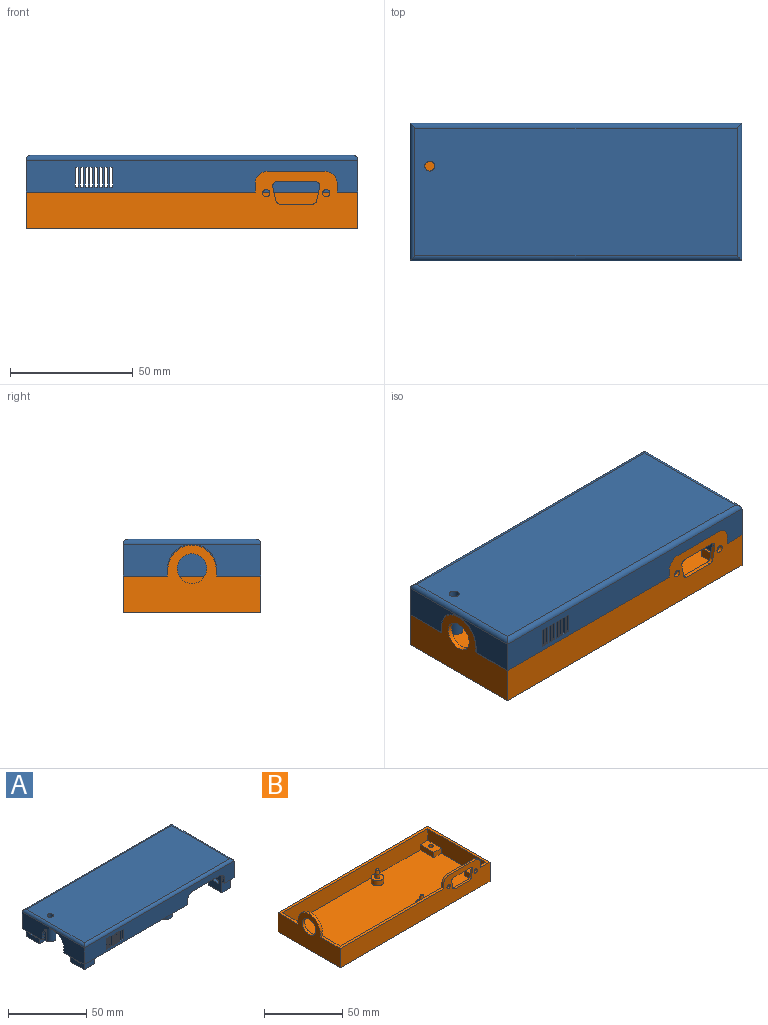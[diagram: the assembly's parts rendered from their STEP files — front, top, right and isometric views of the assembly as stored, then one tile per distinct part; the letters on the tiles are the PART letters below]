
ASSEMBLY  parts=2 mates=1
PART A: 184 faces, bbox 135x56x24 mm
  f0: plane 12x6mm, normal (-1,0,0), area 57.2mm2, adj f16,f36,f37,f132,f133,f134,f151
  f1: plane 12x6mm, normal (-1,0,0), area 57.2mm2, adj f8,f40,f41,f137,f138,f139,f156
  f2: cylinder r=1.55mm len=3.4mm, axis (0,0,-1), area 33.1mm2, adj f137,f155
  f3: cylinder r=1.55mm len=3.4mm, axis (0,0,-1), area 33.1mm2, adj f132,f150
  f4: plane 21x12mm, normal (-1,0,0), area 237.2mm2, adj f11,f19,f113,f114,f120,f121,f124,f125
  f5: plane 21x12.52mm, normal (-1,0,0), area 248mm2, adj f10,f19,f116,f118,f126,f127,f128,f129
  f6: cylinder r=1.6mm len=5.4mm, axis (0,0,1), area 54.3mm2, adj f128,f160
  f7: cylinder r=1.6mm len=5.4mm, axis (0,0,1), area 54.3mm2, adj f124,f165
  f8: plane 135x56mm, normal (0,0,-1), area 435.6mm2, adj f1,f9,f10,f12,f13,f14,f15,f17
  f9: plane 27.48x13mm, normal (-1,0,0), area 357.3mm2, adj f8,f19,f113,f118
  f10: plane 114.5x13mm, normal (0,-1,0), area 1411.7mm2, adj f5,f8,f19,f42,f80,f81,f82,f83
  f11: plane 114.5x13mm, normal (0,1,0), area 1144.9mm2, adj f4,f16,f19,f23,f25,f26,f27,f38
  f12: plane 135x13mm, normal (0,1,0), area 1678.2mm2, adj f8,f15,f17,f28,f80,f81,f82,f83
  f13: plane 135x13mm, normal (0,-1,0), area 1408.4mm2, adj f8,f15,f16,f17,f23,f24,f25,f26
  f14: plane 28x13mm, normal (1,0,0), area 158mm2, adj f8,f16,f19,f20,f21,f22,f37,f41
  f15: plane 56x13mm, normal (-1,0,0), area 522mm2, adj f8,f12,f13,f16,f20,f21,f22,f29
  f16: plane 93.2x17.7mm, normal (0,0,-1), area 255.7mm2, adj f0,f11,f13,f14,f15,f23,f36,f133
  f17: plane 56x13mm, normal (1,0,0), area 728mm2, adj f8,f12,f13,f30
  f18: plane 131x52mm, normal (0,0,1), area 6799.4mm2, adj f28,f29,f30,f31,f180
  f19: plane 131x52mm, normal (0,0,-1), area 6268.1mm2, adj f4,f5,f9,f10,f11,f14,f32,f34
  f20: cylinder r=9.8mm len=19.6mm, axis (-1,0,0), area 61.6mm2, adj f14,f15,f21,f22
  f21: plane 2.3x2mm, normal (0,-1,0), area 4.6mm2, adj f14,f15,f20,f178
  f22: plane 2.3x2mm, normal (0,1,0), area 4.6mm2, adj f14,f15,f20,f179
  f23: plane 3.4x2mm, normal (1,0,0), area 6.8mm2, adj f11,f13,f16,f27
  f24: plane 3.4x2mm, normal (-1,0,0), area 6.8mm2, adj f8,f13,f25,f114
  f25: cylinder r=5mm len=5mm, axis (0,-1,0), area 15.7mm2, adj f11,f13,f24,f26,f114
  f26: plane 23.4x2mm, normal (0,0,-1), area 46.8mm2, adj f11,f13,f25,f27
  f27: cylinder r=5mm len=5mm, axis (0,-1,0), area 15.7mm2, adj f11,f13,f23,f26
  f28: cylinder r=2mm len=135mm, axis (1,0,0), area 419.5mm2, adj f12,f18,f29,f30
  f29: cylinder r=2mm len=56mm, axis (0,1,0), area 171.4mm2, adj f15,f18,f28,f31
  f30: cylinder r=2mm len=56mm, axis (0,-1,0), area 171.4mm2, adj f17,f18,f28,f31
  f31: cylinder r=2mm len=135mm, axis (-1,0,0), area 419.5mm2, adj f13,f18,f29,f30
  f32: cylinder r=4mm len=20mm, axis (0,0,1), area 496.3mm2, adj f19,f33,f174,f175
  f33: plane 8x8mm, normal (0,0,-1), area 42.2mm2, adj f32,f46
  f34: cylinder r=4mm len=20mm, axis (0,0,1), area 496.3mm2, adj f19,f35,f176,f177
  f35: plane 8x8mm, normal (0,0,-1), area 42.2mm2, adj f34,f44
  f36: plane 9.5x6mm, normal (0,-1,0), area 57mm2, adj f0,f16,f38,f152
  f37: plane 19x9.5mm, normal (0,1,0), area 180.5mm2, adj f0,f14,f19,f38,f153
  f38: plane 19x12mm, normal (1,0,0), area 224.9mm2, adj f11,f19,f36,f37,f154,f171
  f39: plane 10x7.5mm, normal (0,0,-1), area 54.6mm2, adj f150,f151,f152,f153,f154
  f40: plane 9.5x6mm, normal (0,1,0), area 57mm2, adj f1,f8,f42,f157
  f41: plane 19x9.5mm, normal (0,-1,0), area 68.5mm2, adj f1,f14,f19,f42,f158,f182,f183
  f42: plane 19x15.5mm, normal (1,0,0), area 280.9mm2, adj f10,f19,f40,f41,f159,f170,f181,f183
  f43: plane 10x7.5mm, normal (0,0,-1), area 54.6mm2, adj f155,f156,f157,f158,f159
  f44: cylinder r=1.6mm len=15mm, axis (0,0,-1), area 144.2mm2, adj f35,f45,f176,f177
  f45: plane 3.2x3.2mm, normal (0,0,-1), area 8mm2, adj f44
  f46: cylinder r=1.6mm len=15mm, axis (0,0,-1), area 144.2mm2, adj f33,f47,f174,f175
  f47: plane 3.2x3.2mm, normal (0,0,-1), area 8mm2, adj f46
  f48: plane 2x1.2mm, normal (0,0,-1), area 2.4mm2, adj f11,f13,f49,f51
  f49: plane 8x2mm, normal (1,0,0), area 16mm2, adj f11,f13,f48,f50
  f50: plane 2x1.2mm, normal (0,0,1), area 2.4mm2, adj f11,f13,f49,f51
  f51: plane 8x2mm, normal (-1,0,0), area 16mm2, adj f11,f13,f48,f50
  f52: plane 2x1.2mm, normal (0,0,-1), area 2.4mm2, adj f11,f13,f53,f55
  f53: plane 8x2mm, normal (1,0,0), area 16mm2, adj f11,f13,f52,f54
  f54: plane 2x1.2mm, normal (0,0,1), area 2.4mm2, adj f11,f13,f53,f55
  f55: plane 8x2mm, normal (-1,0,0), area 16mm2, adj f11,f13,f52,f54
  f56: plane 2x1.2mm, normal (0,0,-1), area 2.4mm2, adj f11,f13,f57,f59
  f57: plane 8x2mm, normal (1,0,0), area 16mm2, adj f11,f13,f56,f58
  f58: plane 2x1.2mm, normal (0,0,1), area 2.4mm2, adj f11,f13,f57,f59
  f59: plane 8x2mm, normal (-1,0,0), area 16mm2, adj f11,f13,f56,f58
  f60: plane 2x1.2mm, normal (0,0,-1), area 2.4mm2, adj f11,f13,f61,f63
  f61: plane 8x2mm, normal (1,0,0), area 16mm2, adj f11,f13,f60,f62
  f62: plane 2x1.2mm, normal (0,0,1), area 2.4mm2, adj f11,f13,f61,f63
  f63: plane 8x2mm, normal (-1,0,0), area 16mm2, adj f11,f13,f60,f62
  f64: plane 2x1.2mm, normal (0,0,-1), area 2.4mm2, adj f11,f13,f65,f67
  f65: plane 8x2mm, normal (1,0,0), area 16mm2, adj f11,f13,f64,f66
  f66: plane 2x1.2mm, normal (0,0,1), area 2.4mm2, adj f11,f13,f65,f67
  f67: plane 8x2mm, normal (-1,0,0), area 16mm2, adj f11,f13,f64,f66
  f68: plane 2x1.2mm, normal (0,0,-1), area 2.4mm2, adj f11,f13,f69,f71
  f69: plane 8x2mm, normal (1,0,0), area 16mm2, adj f11,f13,f68,f70
  f70: plane 2x1.2mm, normal (0,0,1), area 2.4mm2, adj f11,f13,f69,f71
  f71: plane 8x2mm, normal (-1,0,0), area 16mm2, adj f11,f13,f68,f70
  f72: plane 2x1.2mm, normal (0,0,-1), area 2.4mm2, adj f11,f13,f73,f75
  f73: plane 8x2mm, normal (1,0,0), area 16mm2, adj f11,f13,f72,f74
  f74: plane 2x1.2mm, normal (0,0,1), area 2.4mm2, adj f11,f13,f73,f75
  f75: plane 8x2mm, normal (-1,0,0), area 16mm2, adj f11,f13,f72,f74
  f76: plane 8x2mm, normal (1,0,0), area 16mm2, adj f11,f13,f77,f79
  f77: plane 2x1.2mm, normal (0,0,1), area 2.4mm2, adj f11,f13,f76,f78
  f78: plane 8x2mm, normal (-1,0,0), area 16mm2, adj f11,f13,f77,f79
  f79: plane 2x1.2mm, normal (0,0,-1), area 2.4mm2, adj f11,f13,f76,f78
  f80: plane 8x2mm, normal (-1,0,0), area 16mm2, adj f10,f12,f81,f83
  f81: plane 2x1.2mm, normal (0,0,1), area 2.4mm2, adj f10,f12,f80,f82
  f82: plane 8x2mm, normal (1,0,0), area 16mm2, adj f10,f12,f81,f83
  f83: plane 2x1.2mm, normal (0,0,-1), area 2.4mm2, adj f10,f12,f80,f82
  f84: plane 8x2mm, normal (-1,0,0), area 16mm2, adj f10,f12,f85,f87
  f85: plane 2x1.2mm, normal (0,0,1), area 2.4mm2, adj f10,f12,f84,f86
  f86: plane 8x2mm, normal (1,0,0), area 16mm2, adj f10,f12,f85,f87
  f87: plane 2x1.2mm, normal (0,0,-1), area 2.4mm2, adj f10,f12,f84,f86
  f88: plane 8x2mm, normal (-1,0,0), area 16mm2, adj f10,f12,f89,f91
  f89: plane 2x1.2mm, normal (0,0,1), area 2.4mm2, adj f10,f12,f88,f90
  f90: plane 8x2mm, normal (1,0,0), area 16mm2, adj f10,f12,f89,f91
  f91: plane 2x1.2mm, normal (0,0,-1), area 2.4mm2, adj f10,f12,f88,f90
  f92: plane 8x2mm, normal (-1,0,0), area 16mm2, adj f10,f12,f93,f95
  f93: plane 2x1.2mm, normal (0,0,1), area 2.4mm2, adj f10,f12,f92,f94
  f94: plane 8x2mm, normal (1,0,0), area 16mm2, adj f10,f12,f93,f95
  f95: plane 2x1.2mm, normal (0,0,-1), area 2.4mm2, adj f10,f12,f92,f94
  f96: plane 8x2mm, normal (-1,0,0), area 16mm2, adj f10,f12,f97,f99
  f97: plane 2x1.2mm, normal (0,0,1), area 2.4mm2, adj f10,f12,f96,f98
  f98: plane 8x2mm, normal (1,0,0), area 16mm2, adj f10,f12,f97,f99
  f99: plane 2x1.2mm, normal (0,0,-1), area 2.4mm2, adj f10,f12,f96,f98
  f100: plane 8x2mm, normal (-1,0,0), area 16mm2, adj f10,f12,f101,f103
  f101: plane 2x1.2mm, normal (0,0,1), area 2.4mm2, adj f10,f12,f100,f102
  f102: plane 8x2mm, normal (1,0,0), area 16mm2, adj f10,f12,f101,f103
  f103: plane 2x1.2mm, normal (0,0,-1), area 2.4mm2, adj f10,f12,f100,f102
  f104: plane 8x2mm, normal (-1,0,0), area 16mm2, adj f10,f12,f105,f107
  f105: plane 2x1.2mm, normal (0,0,1), area 2.4mm2, adj f10,f12,f104,f106
  f106: plane 8x2mm, normal (1,0,0), area 16mm2, adj f10,f12,f105,f107
  f107: plane 2x1.2mm, normal (0,0,-1), area 2.4mm2, adj f10,f12,f104,f106
  f108: plane 2x1.2mm, normal (0,0,-1), area 2.4mm2, adj f10,f12,f109,f111
  f109: plane 8x2mm, normal (-1,0,0), area 16mm2, adj f10,f12,f108,f110
  f110: plane 2x1.2mm, normal (0,0,1), area 2.4mm2, adj f10,f12,f109,f111
  f111: plane 8x2mm, normal (1,0,0), area 16mm2, adj f10,f12,f108,f110
  f112: plane 12x8mm, normal (1,0,0), area 92.9mm2, adj f8,f113,f114,f168,f173
  f113: plane 21x8mm, normal (0,1,0), area 155mm2, adj f4,f8,f9,f19,f112,f169
  f114: plane 13.78x8mm, normal (0,-1,0), area 67mm2, adj f4,f8,f24,f25,f112,f166
  f115: plane 10x6mm, normal (0,0,-1), area 38.8mm2, adj f165,f166,f167,f168,f169
  f116: plane 8x8mm, normal (0,1,0), area 64mm2, adj f5,f8,f117,f161
  f117: plane 12.52x8mm, normal (1,0,0), area 97mm2, adj f8,f116,f118,f163,f172
  f118: plane 21x8mm, normal (0,-1,0), area 155mm2, adj f5,f8,f9,f19,f117,f164
  f119: plane 10.52x6mm, normal (0,0,-1), area 41.9mm2, adj f160,f161,f162,f163,f164
  f120: plane 5.65x2.6mm, normal (0,-1,0), area 14.7mm2, adj f4,f123,f124,f125
  f121: plane 5.65x2.6mm, normal (0,1,0), area 14.7mm2, adj f4,f122,f124,f125
  f122: plane 2.85x2.6mm, normal (-0.87,0.5,0), area 6.7mm2, adj f121,f123,f124,f125,f173
  f123: plane 2.85x2.6mm, normal (-0.87,-0.5,0), area 6.7mm2, adj f120,f122,f124,f125,f173
  f124: plane 7.29x5.7mm, normal (0,0,1), area 28.8mm2, adj f4,f7,f120,f121,f122,f123
  f125: plane 7.29x5.7mm, normal (0,0,-1), area 28.8mm2, adj f4,f120,f121,f122,f123,f143
  f126: plane 5.65x2.6mm, normal (0,-1,0), area 14.7mm2, adj f5,f128,f129,f131
  f127: plane 5.65x2.6mm, normal (0,1,0), area 14.7mm2, adj f5,f128,f129,f130
  f128: plane 7.29x5.7mm, normal (0,0,1), area 28.8mm2, adj f5,f6,f126,f127,f130,f131
  f129: plane 7.29x5.7mm, normal (0,0,-1), area 28.8mm2, adj f5,f126,f127,f130,f131,f145
  f130: plane 2.85x2.6mm, normal (-0.87,0.5,0), area 6.7mm2, adj f127,f128,f129,f131,f172
  f131: plane 2.85x2.6mm, normal (-0.87,-0.5,0), area 6.7mm2, adj f126,f128,f129,f130,f172
  f132: plane 8.79x5.7mm, normal (0,0,1), area 37.9mm2, adj f0,f3,f133,f134,f135,f136
  f133: plane 7.15x2.6mm, normal (0,-1,0), area 18.6mm2, adj f0,f16,f132,f136
  f134: plane 7.15x2.6mm, normal (0,1,0), area 18.6mm2, adj f0,f16,f132,f135
  f135: plane 2.85x2.6mm, normal (-0.87,0.5,0), area 6.7mm2, adj f16,f132,f134,f136,f171
  f136: plane 2.85x2.6mm, normal (-0.87,-0.5,0), area 6.7mm2, adj f16,f132,f133,f135,f171
  f137: plane 8.79x5.7mm, normal (0,0,1), area 37.9mm2, adj f1,f2,f138,f139,f140,f141
  f138: plane 7.15x2.6mm, normal (0,-1,0), area 18.6mm2, adj f1,f8,f137,f141
  f139: plane 7.15x2.6mm, normal (0,1,0), area 18.6mm2, adj f1,f8,f137,f140
  f140: plane 2.85x2.6mm, normal (-0.87,0.5,0), area 6.7mm2, adj f8,f137,f139,f141,f170
  f141: plane 2.85x2.6mm, normal (-0.87,-0.5,0), area 6.7mm2, adj f8,f137,f138,f140,f170
  f142: plane 3.2x3.2mm, normal (0,0,-1), area 8mm2, adj f143
  f143: cylinder r=1.6mm len=13mm, axis (0,0,1), area 130.7mm2, adj f125,f142
  f144: plane 3.2x3.2mm, normal (0,0,-1), area 8mm2, adj f145
  f145: cylinder r=1.6mm len=13mm, axis (0,0,1), area 130.7mm2, adj f129,f144
  f146: plane 3.1x3.1mm, normal (0,0,-1), area 7.5mm2, adj f147
  f147: cylinder r=1.55mm len=8mm, axis (0,0,-1), area 77.9mm2, adj f16,f146
  f148: plane 3.1x3.1mm, normal (0,0,-1), area 7.5mm2, adj f149
  f149: cylinder r=1.55mm len=8mm, axis (0,0,-1), area 77.9mm2, adj f8,f148
  f150: cone r=1.55mm half-angle=45deg, axis (0,0,-1), area 18.2mm2, adj f3,f39
  f151: plane 12x1mm, normal (-0.71,0,-0.71), area 15.6mm2, adj f0,f39,f152,f153
  f152: plane 9.5x1mm, normal (0,-0.71,-0.71), area 12mm2, adj f36,f39,f151,f154
  f153: plane 9.5x1mm, normal (0,0.71,-0.71), area 12mm2, adj f37,f39,f151,f154
  f154: plane 12x1mm, normal (0.71,0,-0.71), area 15.6mm2, adj f38,f39,f152,f153
  f155: cone r=1.55mm half-angle=45deg, axis (0,0,-1), area 18.2mm2, adj f2,f43
  f156: plane 12x1mm, normal (-0.71,0,-0.71), area 15.6mm2, adj f1,f43,f157,f158
  f157: plane 9.5x1mm, normal (0,0.71,-0.71), area 12mm2, adj f40,f43,f156,f159
  f158: plane 9.5x1mm, normal (0,-0.71,-0.71), area 12mm2, adj f41,f43,f156,f159
  f159: plane 12x1mm, normal (0.71,0,-0.71), area 15.6mm2, adj f42,f43,f157,f158
  f160: cone r=1.6mm half-angle=45deg, axis (0,0,-1), area 18.7mm2, adj f6,f119
  f161: plane 8x1mm, normal (0,0.71,-0.71), area 9.9mm2, adj f116,f119,f162,f163
  f162: plane 12.52x1mm, normal (-0.71,0,-0.71), area 16.3mm2, adj f5,f119,f161,f164
  f163: plane 12.52x1mm, normal (0.71,0,-0.71), area 16.3mm2, adj f117,f119,f161,f164
  f164: plane 8x1mm, normal (0,-0.71,-0.71), area 9.9mm2, adj f118,f119,f162,f163
  f165: cone r=1.6mm half-angle=45deg, axis (0,0,-1), area 18.7mm2, adj f7,f115
  f166: plane 8x1mm, normal (0,-0.71,-0.71), area 9.9mm2, adj f114,f115,f167,f168
  f167: plane 12x1mm, normal (-0.71,0,-0.71), area 15.6mm2, adj f4,f115,f166,f169
  f168: plane 12x1mm, normal (0.71,0,-0.71), area 15.6mm2, adj f112,f115,f166,f169
  f169: plane 8x1mm, normal (0,0.71,-0.71), area 9.9mm2, adj f113,f115,f167,f168
  f170: cylinder r=1mm len=2mm, axis (-1,0,0), area 6.8mm2, adj f42,f140,f141
  f171: cylinder r=1mm len=2mm, axis (-1,0,0), area 6.8mm2, adj f38,f135,f136
  f172: cylinder r=1mm len=2mm, axis (-1,0,0), area 6.8mm2, adj f117,f130,f131
  f173: cylinder r=1mm len=2mm, axis (-1,0,0), area 6.8mm2, adj f112,f122,f123
  f174: cylinder r=1mm len=2.75mm, axis (-1,0,0), area 15.8mm2, adj f32,f46
  f175: cylinder r=1mm len=2.75mm, axis (-1,0,0), area 15.8mm2, adj f32,f46
  f176: cylinder r=1mm len=2.75mm, axis (-1,0,0), area 15.8mm2, adj f34,f44
  f177: cylinder r=1mm len=2.75mm, axis (-1,0,0), area 15.8mm2, adj f34,f44
  f178: plane 2x0.5mm, normal (0,-0.71,-0.71), area 1.4mm2, adj f8,f14,f15,f21
  f179: plane 2x0.5mm, normal (0,0.71,-0.71), area 1.4mm2, adj f14,f15,f16,f22
  f180: cylinder r=2mm len=18mm, axis (0,0,-1), area 226.2mm2, adj f18,f183
  f181: cylinder r=3.5mm len=16mm, axis (0,0,1), area 175.9mm2, adj f19,f42,f182,f183
  f182: plane 16x3.5mm, normal (-1,0,0), area 56mm2, adj f19,f41,f181,f183
  f183: plane 7x7mm, normal (0,0,-1), area 31.2mm2, adj f41,f42,f180,f181,f182
PART B: 69 faces, bbox 135x56x28 mm
  f0: cylinder r=1.55mm len=3.1mm, axis (0,0,-1), area 19.5mm2, adj f58,f65
  f1: cylinder r=1.55mm len=3.1mm, axis (0,0,-1), area 19.5mm2, adj f55,f63
  f2: cylinder r=1.55mm len=3.1mm, axis (0,0,-1), area 19.5mm2, adj f48,f61
  f3: cylinder r=1.55mm len=3.1mm, axis (0,0,-1), area 19.5mm2, adj f46,f59
  f4: plane 131x52mm, normal (0,0,1), area 6440.1mm2, adj f5,f6,f7,f36,f37,f41,f45,f47
  f5: plane 131x13mm, normal (0,1,0), area 1385.1mm2, adj f4,f6,f25,f26,f27,f28,f29,f30
  f6: plane 52x13mm, normal (-1,0,0), area 578.4mm2, adj f4,f5,f7,f31,f54,f55,f56,f58
  f7: plane 131x13mm, normal (0,-1,0), area 1675mm2, adj f4,f6,f31,f36,f53,f55
  f8: plane 3.4x1.5mm, normal (1,0,0), area 5.1mm2, adj f10,f23,f24,f31
  f9: plane 3.4x1.5mm, normal (-1,0,0), area 5.1mm2, adj f12,f23,f24,f30
  f10: cylinder r=5mm len=5mm, axis (0,-1,0), area 11.8mm2, adj f8,f11,f23,f24
  f11: plane 23.4x1.5mm, normal (0,0,1), area 35.1mm2, adj f10,f12,f23,f24
  f12: cylinder r=5mm len=5mm, axis (0,-1,0), area 11.8mm2, adj f9,f11,f23,f24
  f13: cylinder r=2mm len=1.96mm, axis (0,-1,0), area 4.1mm2, adj f14,f21,f23,f24
  f14: plane 5.4x1.5mm, normal (0.98,0,0.21), area 8.3mm2, adj f13,f15,f23,f24
  f15: cylinder r=2mm len=2.42mm, axis (0,-1,0), area 5.3mm2, adj f14,f16,f23,f24
  f16: plane 15.06x1.5mm, normal (0,0,-1), area 22.6mm2, adj f15,f17,f23,f24
  f17: cylinder r=2mm len=2.42mm, axis (0,-1,0), area 5.3mm2, adj f16,f18,f23,f24
  f18: plane 5.4x1.5mm, normal (-0.98,0,0.21), area 8.3mm2, adj f17,f19,f23,f24
  f19: cylinder r=2mm len=1.96mm, axis (0,-1,0), area 4.1mm2, adj f18,f21,f23,f24
  f20: cylinder r=1.5mm len=3mm, axis (0,-1,0), area 14.1mm2, adj f23,f24
  f21: plane 12.76x1.5mm, normal (0,0,1), area 19.1mm2, adj f13,f19,f23,f24
  f22: cylinder r=1.5mm len=3mm, axis (0,-1,0), area 14.1mm2, adj f23,f24
  f23: plane 33.4x17.4mm, normal (0,1,0), area 380.2mm2, adj f8,f9,f10,f11,f12,f13,f14,f15
  f24: plane 135x23.4mm, normal (0,-1,0), area 2115.3mm2, adj f8,f9,f10,f11,f12,f13,f14,f15
  f25: plane 4x0.5mm, normal (-1,0,0), area 2mm2, adj f5,f23,f29,f31
  f26: plane 4x0.5mm, normal (1,0,0), area 2mm2, adj f5,f23,f28,f30
  f27: plane 23.4x0.5mm, normal (0,0,1), area 11.7mm2, adj f5,f23,f28,f29
  f28: cylinder r=5mm len=5mm, axis (0,-1,0), area 3.9mm2, adj f5,f23,f26,f27
  f29: cylinder r=5mm len=5mm, axis (0,-1,0), area 3.9mm2, adj f5,f23,f25,f27
  f30: plane 93.2x18mm, normal (0,0,1), area 218.4mm2, adj f5,f9,f24,f26,f32,f36,f50
  f31: plane 135x56mm, normal (0,0,1), area 422.8mm2, adj f5,f6,f7,f8,f24,f25,f32,f33
  f32: plane 56x28mm, normal (-1,0,0), area 944mm2, adj f24,f30,f31,f34,f35,f49,f50,f51
  f33: plane 56x15mm, normal (1,0,0), area 840mm2, adj f24,f31,f34,f35
  f34: plane 135x15mm, normal (0,1,0), area 2025mm2, adj f31,f32,f33,f35
  f35: plane 135x56mm, normal (0,0,-1), area 7457.9mm2, adj f24,f32,f33,f34,f60,f62,f64,f66
  f36: plane 52x26mm, normal (1,0,0), area 780mm2, adj f4,f5,f7,f30,f31,f49,f50,f51
  f37: cylinder r=4mm len=8mm, axis (0,0,-1), area 100.5mm2, adj f4,f38
  f38: plane 8x8mm, normal (0,0,1), area 43.2mm2, adj f37,f40
  f39: plane 2x2mm, normal (0,0,1), area 3.1mm2, adj f68
  f40: cylinder r=1.5mm len=3.16mm, axis (0,0,-1), area 29.8mm2, adj f38,f68
  f41: cylinder r=4mm len=8mm, axis (0,0,-1), area 100.5mm2, adj f4,f42
  f42: plane 8x8mm, normal (0,0,1), area 43.2mm2, adj f41,f44
  f43: plane 2x2mm, normal (0,0,1), area 3.1mm2, adj f67
  f44: cylinder r=1.5mm len=3.16mm, axis (0,0,-1), area 29.8mm2, adj f42,f67
  f45: cylinder r=4mm len=8mm, axis (0,0,-1), area 100.5mm2, adj f4,f46
  f46: plane 8x8mm, normal (0,0,1), area 42.7mm2, adj f3,f45
  f47: cylinder r=4mm len=8mm, axis (0,0,-1), area 100.5mm2, adj f4,f48
  f48: plane 8x8mm, normal (0,0,1), area 42.7mm2, adj f2,f47
  f49: cylinder r=6mm len=12mm, axis (-1,0,0), area 75.4mm2, adj f32,f36
  f50: plane 3x2mm, normal (0,-1,0), area 6mm2, adj f30,f32,f36,f51
  f51: cylinder r=10mm len=20mm, axis (-1,0,0), area 62.8mm2, adj f32,f36,f50,f52
  f52: plane 3x2mm, normal (0,1,0), area 6mm2, adj f31,f32,f36,f51
  f53: plane 12.2x4mm, normal (-1,0,0), area 48.8mm2, adj f4,f7,f54,f55
  f54: plane 7x4mm, normal (0,-1,0), area 28mm2, adj f4,f6,f53,f55
  f55: plane 12.2x7mm, normal (0,0,1), area 77.9mm2, adj f1,f6,f7,f53,f54
  f56: plane 7x4mm, normal (0,1,0), area 28mm2, adj f4,f6,f57,f58
  f57: plane 12.2x4mm, normal (-1,0,0), area 48.8mm2, adj f4,f5,f56,f58
  f58: plane 12.2x7mm, normal (0,0,1), area 77.9mm2, adj f0,f5,f6,f56,f57
  f59: plane 5.7x5.7mm, normal (0,0,-1), area 18mm2, adj f3,f60
  f60: cylinder r=2.85mm len=5.7mm, axis (0,0,-1), area 71.6mm2, adj f35,f59
  f61: plane 5.7x5.7mm, normal (0,0,-1), area 18mm2, adj f2,f62
  f62: cylinder r=2.85mm len=5.7mm, axis (0,0,-1), area 71.6mm2, adj f35,f61
  f63: plane 5.7x5.7mm, normal (0,0,-1), area 18mm2, adj f1,f64
  f64: cylinder r=2.85mm len=5.7mm, axis (0,0,-1), area 71.6mm2, adj f35,f63
  f65: plane 5.7x5.7mm, normal (0,0,-1), area 18mm2, adj f0,f66
  f66: cylinder r=2.85mm len=5.7mm, axis (0,0,-1), area 71.6mm2, adj f35,f65
  f67: cone r=1mm half-angle=10deg, axis (0,0,-1), area 22.6mm2, adj f43,f44
  f68: cone r=1mm half-angle=10deg, axis (0,0,-1), area 22.6mm2, adj f39,f40
PLACE A t=(-7.49,15.71,-72.24)mm
PLACE B t=(-7.49,15.71,-37.24)mm
MATE cylindrical A.f34 <-> B.f41  axis (0,0,1) through (74.01,23.71,-29.24)mm
